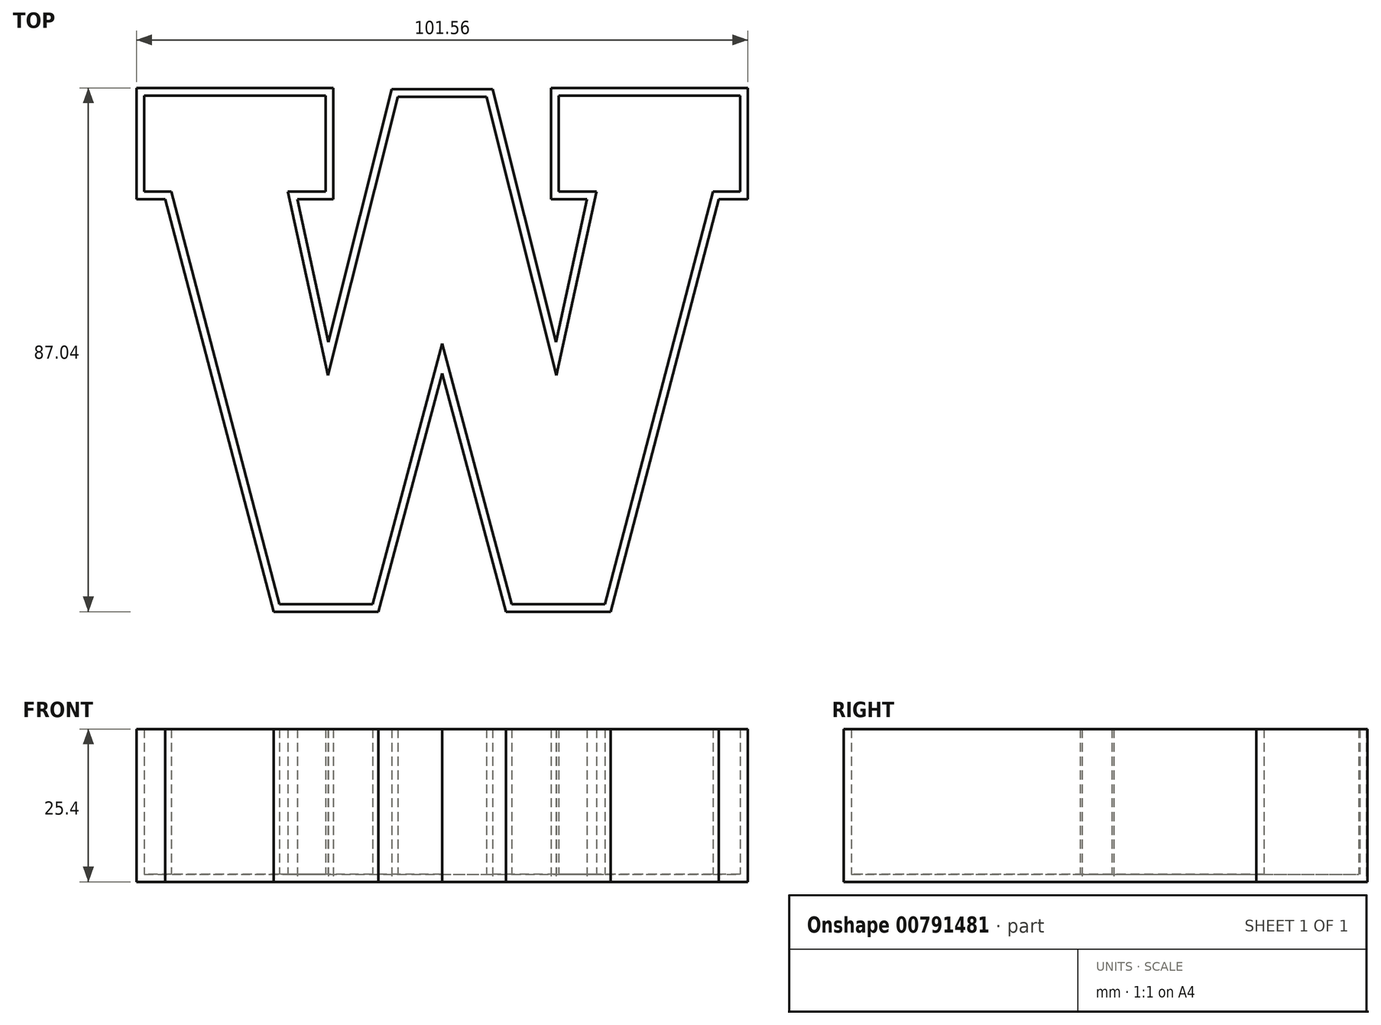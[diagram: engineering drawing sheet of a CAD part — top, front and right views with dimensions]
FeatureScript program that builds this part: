
annotation { "Feature Type Name" : "Feature", "Feature Type Description" : "" }
export const myFeature = defineFeature(function(context is Context, id is Id, definition is map)
    precondition{}
    {
        {
            var Q0;
            Q0=qCreatedBy(makeId("Top.planeOp"),FACE);
            var sketch = newSketch(context, id + "F0", { "sketchPlane" : qUnion([Q0])});
            skLineSegment(sketch, "E0", {"start": v(0, -2.34) * mm, "end": v(-10.6, -41.95) * mm});
            skLineSegment(sketch, "E1", {"start": v(-10.6, -41.95) * mm, "end": v(-28.02, -41.95) * mm});
            skLineSegment(sketch, "E2", {"start": v(-28.02, -41.95) * mm, "end": v(-46, 26.6) * mm});
            skLineSegment(sketch, "E3", {"start": v(-46, 26.6) * mm, "end": v(-50.78, 26.6) * mm});
            skLineSegment(sketch, "E4", {"start": v(-50.78, 26.6) * mm, "end": v(-50.78, 45.09) * mm});
            skLineSegment(sketch, "E5", {"start": v(-50.78, 45.09) * mm, "end": v(-18.1, 45.09) * mm});
            skLineSegment(sketch, "E6", {"start": v(-18.1, 45.09) * mm, "end": v(-18.1, 26.6) * mm});
            skLineSegment(sketch, "E7", {"start": v(-18.1, 26.6) * mm, "end": v(-24.09, 26.6) * mm});
            skLineSegment(sketch, "E8", {"start": v(-24.09, 26.6) * mm, "end": v(-18.91, 2.88) * mm});
            skLineSegment(sketch, "E9", {"start": v(-18.91, 2.88) * mm, "end": v(-8.36, 44.89) * mm});
            skLineSegment(sketch, "E10", {"start": v(-8.36, 44.89) * mm, "end": v(3.75, 44.89) * mm});
            skLineSegment(sketch, "E11", {"start": v(0, -2.34) * mm, "end": v(0, 59.6) * mm});
            skLineSegment(sketch, "E12.MirrorCS", {"start": v(8.36, 44.89) * mm, "end": v(-3.75, 44.89) * mm});
            skLineSegment(sketch, "E13.MirrorCS", {"start": v(18.91, 2.88) * mm, "end": v(8.36, 44.89) * mm});
            skLineSegment(sketch, "E14.MirrorCS", {"start": v(24.09, 26.6) * mm, "end": v(18.91, 2.88) * mm});
            skLineSegment(sketch, "E15.MirrorCS", {"start": v(18.1, 45.09) * mm, "end": v(18.1, 26.6) * mm});
            skLineSegment(sketch, "E16.MirrorCS", {"start": v(50.78, 45.09) * mm, "end": v(18.1, 45.09) * mm});
            skLineSegment(sketch, "E17.MirrorCS", {"start": v(50.78, 26.6) * mm, "end": v(50.78, 45.09) * mm});
            skLineSegment(sketch, "E18.MirrorCS", {"start": v(18.1, 26.6) * mm, "end": v(24.09, 26.6) * mm});
            skLineSegment(sketch, "E19.MirrorCS", {"start": v(28.02, -41.95) * mm, "end": v(46, 26.6) * mm});
            skLineSegment(sketch, "E20.MirrorCS", {"start": v(46, 26.6) * mm, "end": v(50.78, 26.6) * mm});
            skLineSegment(sketch, "E21.MirrorCS", {"start": v(10.6, -41.95) * mm, "end": v(28.02, -41.95) * mm});
            skLineSegment(sketch, "E22.MirrorCS", {"start": v(0, -2.34) * mm, "end": v(10.6, -41.95) * mm});
            skSolve(sketch);
        }
        {
            var Q0;
            Q0 = qSketchRegion(id + "F0", true);
            extrude(context, id + "F1", {"entities" : qUnion([Q0]), "depth" : 25.4 * mm, "offsetDistance" : 25.4 * mm});
        }
        {
            var Q0;
            Q0=makeQuery(id+"F1.opExtrude","CAP_FACE",FACE,{"disambiguationData":[OSD([sQuery(id+"F0.wireOp",EDGE,"E0"),sQuery(id+"F0.wireOp",EDGE,"E1"),sQuery(id+"F0.wireOp",EDGE,"E2"),sQuery(id+"F0.wireOp",EDGE,"E3"),sQuery(id+"F0.wireOp",EDGE,"E4"),sQuery(id+"F0.wireOp",EDGE,"E5"),sQuery(id+"F0.wireOp",EDGE,"E6"),sQuery(id+"F0.wireOp",EDGE,"E7"),sQuery(id+"F0.wireOp",EDGE,"E8"),sQuery(id+"F0.wireOp",EDGE,"E9"),sQuery(id+"F0.wireOp",EDGE,"E12.MirrorCS"),sQuery(id+"F0.wireOp",EDGE,"E10"),sQuery(id+"F0.wireOp",EDGE,"E13.MirrorCS"),sQuery(id+"F0.wireOp",EDGE,"E14.MirrorCS"),sQuery(id+"F0.wireOp",EDGE,"E15.MirrorCS"),sQuery(id+"F0.wireOp",EDGE,"E16.MirrorCS"),sQuery(id+"F0.wireOp",EDGE,"E17.MirrorCS"),sQuery(id+"F0.wireOp",EDGE,"E18.MirrorCS"),sQuery(id+"F0.wireOp",EDGE,"E19.MirrorCS"),sQuery(id+"F0.wireOp",EDGE,"E20.MirrorCS"),sQuery(id+"F0.wireOp",EDGE,"E21.MirrorCS"),sQuery(id+"F0.wireOp",EDGE,"E22.MirrorCS")])],"isStart":false});
            shell(context, id + "F2", {"entities" : qUnion([Q0]), "thickness" : 1.27 * mm});
        }
    });
